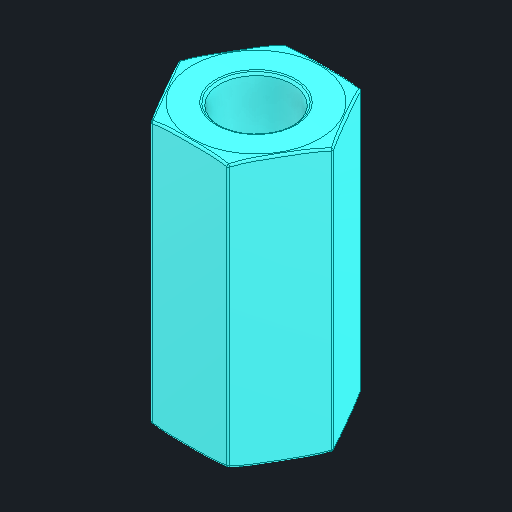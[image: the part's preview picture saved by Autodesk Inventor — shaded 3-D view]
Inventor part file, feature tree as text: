
AUTODESK INVENTOR PART (.ipt)
format: ipt  version: 2025 (Build 290162000, 162)  size: 188,416 bytes
history: native  units: in
note: dims shown in document units (in); Inventor stores cm internally (conversion verified against a paired STEP export)
features: fillet x1
ambient origin geometry x8: Origin, YZ Plane, XZ Plane, XY Plane, X Axis, Y Axis, Z Axis, Center Point
bodies: Solid1 (feature_tree)
feature tree (1):
  fillet  "Fillet1"  [1 undecoded]
note: 1 required parameter value undecoded (feature->parameter linkage not recoverable at this tier; creation-order binding heuristic only, values carry confidence <= 0.55)
